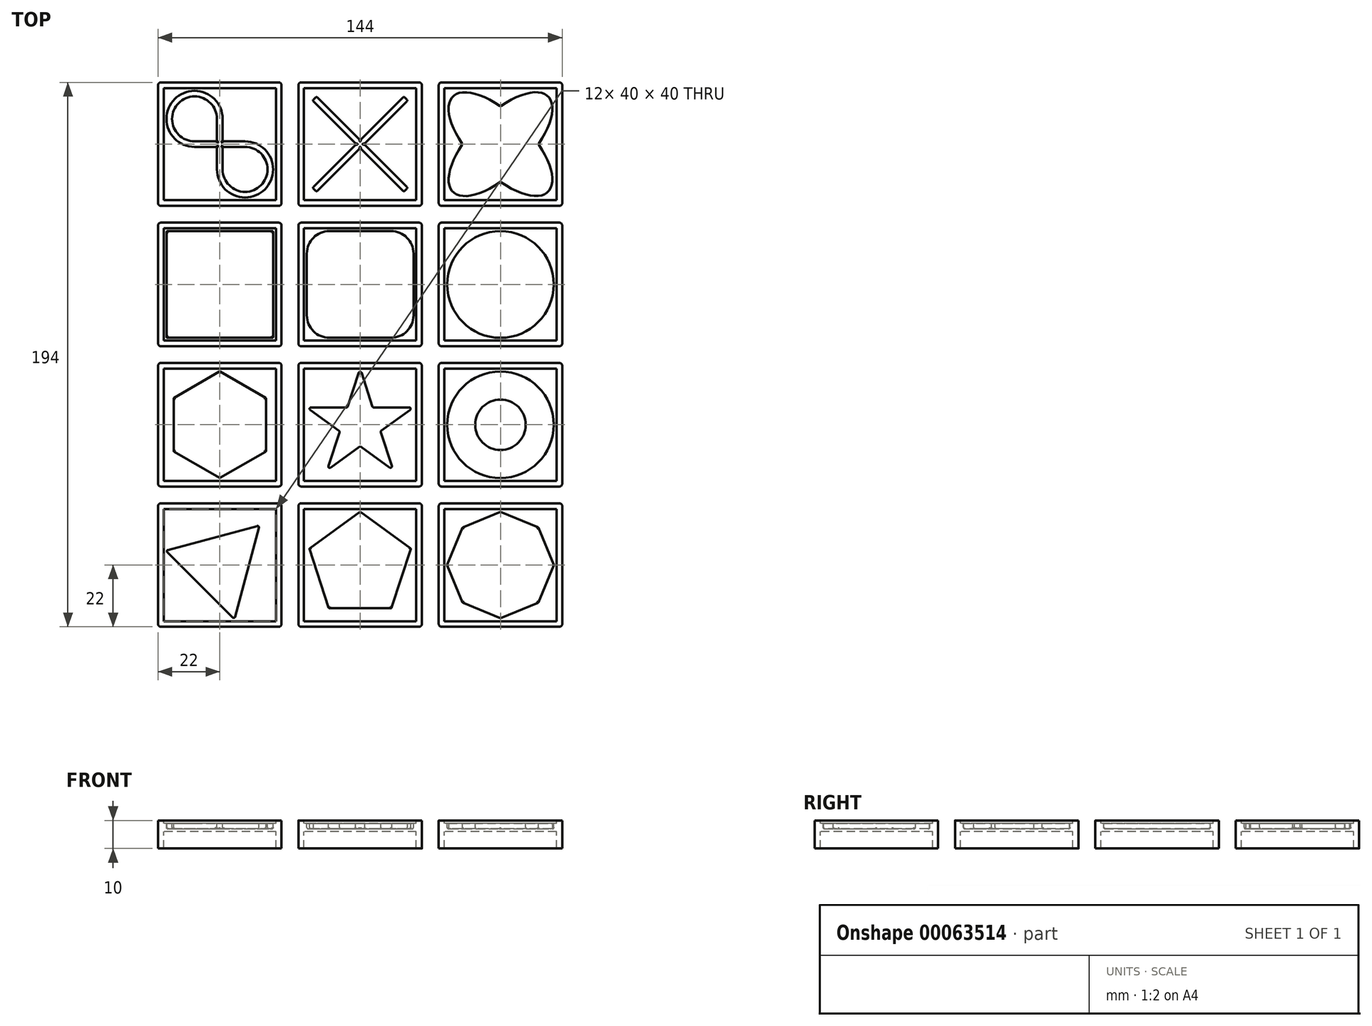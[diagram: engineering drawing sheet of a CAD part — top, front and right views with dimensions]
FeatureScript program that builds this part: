
annotation { "Feature Type Name" : "Feature", "Feature Type Description" : "" }
export const myFeature = defineFeature(function(context is Context, id is Id, definition is map)
    precondition{}
    {
        {
            var Q0;
            Q0=qCreatedBy(makeId("Top.planeOp"),FACE);
            var sketch = newSketch(context, id + "F0", { "sketchPlane" : qUnion([Q0])});
            skLineSegment(sketch, "E0.rect.bottom", {"start": v(20, 20) * mm, "end": v(-20, 20) * mm});
            skLineSegment(sketch, "E0.rect.top", {"start": v(20, -20) * mm, "end": v(-20, -20) * mm});
            skLineSegment(sketch, "E0.rect.left", {"start": v(20, 20) * mm, "end": v(20, -20) * mm});
            skLineSegment(sketch, "E0.rect.right", {"start": v(-20, 20) * mm, "end": v(-20, -20) * mm});
            skPoint(sketch, "E0.rect.middle", {"position": v(0, 0) * mm});
            skLineSegment(sketch, "E1.0.1.0", {"start": v(20, 30) * mm, "end": v(-20, 30) * mm});
            skLineSegment(sketch, "E1.0.1.1", {"start": v(-20, 70) * mm, "end": v(-20, 30) * mm});
            skLineSegment(sketch, "E1.0.1.2", {"start": v(20, 70) * mm, "end": v(-20, 70) * mm});
            skLineSegment(sketch, "E1.0.1.3", {"start": v(20, 70) * mm, "end": v(20, 30) * mm});
            skLineSegment(sketch, "E1.0.2.0", {"start": v(20, 80) * mm, "end": v(-20, 80) * mm});
            skLineSegment(sketch, "E1.0.2.1", {"start": v(-20, 120) * mm, "end": v(-20, 80) * mm});
            skLineSegment(sketch, "E1.0.2.2", {"start": v(20, 120) * mm, "end": v(-20, 120) * mm});
            skLineSegment(sketch, "E1.0.2.3", {"start": v(20, 120) * mm, "end": v(20, 80) * mm});
            skLineSegment(sketch, "E1.1.0.0", {"start": v(70, -20) * mm, "end": v(30, -20) * mm});
            skLineSegment(sketch, "E1.1.0.1", {"start": v(30, 20) * mm, "end": v(30, -20) * mm});
            skLineSegment(sketch, "E1.1.0.2", {"start": v(70, 20) * mm, "end": v(30, 20) * mm});
            skLineSegment(sketch, "E1.1.0.3", {"start": v(70, 20) * mm, "end": v(70, -20) * mm});
            skLineSegment(sketch, "E1.1.1.0", {"start": v(70, 30) * mm, "end": v(30, 30) * mm});
            skLineSegment(sketch, "E1.1.1.1", {"start": v(30, 70) * mm, "end": v(30, 30) * mm});
            skLineSegment(sketch, "E1.1.1.2", {"start": v(70, 70) * mm, "end": v(30, 70) * mm});
            skLineSegment(sketch, "E1.1.1.3", {"start": v(70, 70) * mm, "end": v(70, 30) * mm});
            skLineSegment(sketch, "E1.1.2.0", {"start": v(70, 80) * mm, "end": v(30, 80) * mm});
            skLineSegment(sketch, "E1.1.2.1", {"start": v(30, 120) * mm, "end": v(30, 80) * mm});
            skLineSegment(sketch, "E1.1.2.2", {"start": v(70, 120) * mm, "end": v(30, 120) * mm});
            skLineSegment(sketch, "E1.1.2.3", {"start": v(70, 120) * mm, "end": v(70, 80) * mm});
            skLineSegment(sketch, "E1.2.0.0", {"start": v(120, -20) * mm, "end": v(80, -20) * mm});
            skLineSegment(sketch, "E1.2.0.1", {"start": v(80, 20) * mm, "end": v(80, -20) * mm});
            skLineSegment(sketch, "E1.2.0.2", {"start": v(120, 20) * mm, "end": v(80, 20) * mm});
            skLineSegment(sketch, "E1.2.0.3", {"start": v(120, 20) * mm, "end": v(120, -20) * mm});
            skLineSegment(sketch, "E1.2.1.0", {"start": v(120, 30) * mm, "end": v(80, 30) * mm});
            skLineSegment(sketch, "E1.2.1.1", {"start": v(80, 70) * mm, "end": v(80, 30) * mm});
            skLineSegment(sketch, "E1.2.1.2", {"start": v(120, 70) * mm, "end": v(80, 70) * mm});
            skLineSegment(sketch, "E1.2.1.3", {"start": v(120, 70) * mm, "end": v(120, 30) * mm});
            skLineSegment(sketch, "E1.2.2.0", {"start": v(120, 80) * mm, "end": v(80, 80) * mm});
            skLineSegment(sketch, "E1.2.2.1", {"start": v(80, 120) * mm, "end": v(80, 80) * mm});
            skLineSegment(sketch, "E1.2.2.2", {"start": v(120, 120) * mm, "end": v(80, 120) * mm});
            skLineSegment(sketch, "E1.2.2.3", {"start": v(120, 120) * mm, "end": v(120, 80) * mm});
            skLineSegment(sketch, "E1.direction1", {"start": v(-20, -20) * mm, "end": v(30, -20) * mm, "construction": true});
            skLineSegment(sketch, "E1.direction2", {"start": v(-20, -20) * mm, "end": v(-20, 30) * mm, "construction": true});
            skLineSegment(sketch, "E2", {"start": v(-22, 122) * mm, "end": v(-20, 120) * mm, "construction": true});
            skLineSegment(sketch, "E3", {"start": v(120, -20) * mm, "end": v(122, -22) * mm, "construction": true});
            skLineSegment(sketch, "E4", {"start": v(122, 122) * mm, "end": v(120, 120) * mm, "construction": true});
            skLineSegment(sketch, "E5.0", {"start": v(-22, 22) * mm, "end": v(-22, -22) * mm});
            skLineSegment(sketch, "E5.1", {"start": v(22, 22) * mm, "end": v(-22, 22) * mm});
            skLineSegment(sketch, "E5.2", {"start": v(22, 22) * mm, "end": v(22, -22) * mm});
            skLineSegment(sketch, "E5.3", {"start": v(22, -22) * mm, "end": v(-22, -22) * mm});
            skLineSegment(sketch, "E6.0.1.0", {"start": v(-22, 72) * mm, "end": v(-22, 28) * mm});
            skLineSegment(sketch, "E6.0.1.1", {"start": v(22, 28) * mm, "end": v(-22, 28) * mm});
            skLineSegment(sketch, "E6.0.1.2", {"start": v(22, 72) * mm, "end": v(22, 28) * mm});
            skLineSegment(sketch, "E6.0.1.3", {"start": v(22, 72) * mm, "end": v(-22, 72) * mm});
            skLineSegment(sketch, "E6.0.2.0", {"start": v(-22, 122) * mm, "end": v(-22, 78) * mm});
            skLineSegment(sketch, "E6.0.2.1", {"start": v(22, 78) * mm, "end": v(-22, 78) * mm});
            skLineSegment(sketch, "E6.0.2.2", {"start": v(22, 122) * mm, "end": v(22, 78) * mm});
            skLineSegment(sketch, "E6.0.2.3", {"start": v(22, 122) * mm, "end": v(-22, 122) * mm});
            skLineSegment(sketch, "E6.1.0.0", {"start": v(28, 22) * mm, "end": v(28, -22) * mm});
            skLineSegment(sketch, "E6.1.0.1", {"start": v(72, -22) * mm, "end": v(28, -22) * mm});
            skLineSegment(sketch, "E6.1.0.2", {"start": v(72, 22) * mm, "end": v(72, -22) * mm});
            skLineSegment(sketch, "E6.1.0.3", {"start": v(72, 22) * mm, "end": v(28, 22) * mm});
            skLineSegment(sketch, "E6.1.1.0", {"start": v(28, 72) * mm, "end": v(28, 28) * mm});
            skLineSegment(sketch, "E6.1.1.1", {"start": v(72, 28) * mm, "end": v(28, 28) * mm});
            skLineSegment(sketch, "E6.1.1.2", {"start": v(72, 72) * mm, "end": v(72, 28) * mm});
            skLineSegment(sketch, "E6.1.1.3", {"start": v(72, 72) * mm, "end": v(28, 72) * mm});
            skLineSegment(sketch, "E6.1.2.0", {"start": v(28, 122) * mm, "end": v(28, 78) * mm});
            skLineSegment(sketch, "E6.1.2.1", {"start": v(72, 78) * mm, "end": v(28, 78) * mm});
            skLineSegment(sketch, "E6.1.2.2", {"start": v(72, 122) * mm, "end": v(72, 78) * mm});
            skLineSegment(sketch, "E6.1.2.3", {"start": v(72, 122) * mm, "end": v(28, 122) * mm});
            skLineSegment(sketch, "E6.2.0.0", {"start": v(78, 22) * mm, "end": v(78, -22) * mm});
            skLineSegment(sketch, "E6.2.0.1", {"start": v(122, -22) * mm, "end": v(78, -22) * mm});
            skLineSegment(sketch, "E6.2.0.2", {"start": v(122, 22) * mm, "end": v(122, -22) * mm});
            skLineSegment(sketch, "E6.2.0.3", {"start": v(122, 22) * mm, "end": v(78, 22) * mm});
            skLineSegment(sketch, "E6.2.1.0", {"start": v(78, 72) * mm, "end": v(78, 28) * mm});
            skLineSegment(sketch, "E6.2.1.1", {"start": v(122, 28) * mm, "end": v(78, 28) * mm});
            skLineSegment(sketch, "E6.2.1.2", {"start": v(122, 72) * mm, "end": v(122, 28) * mm});
            skLineSegment(sketch, "E6.2.1.3", {"start": v(122, 72) * mm, "end": v(78, 72) * mm});
            skLineSegment(sketch, "E6.2.2.0", {"start": v(78, 122) * mm, "end": v(78, 78) * mm});
            skLineSegment(sketch, "E6.2.2.1", {"start": v(122, 78) * mm, "end": v(78, 78) * mm});
            skLineSegment(sketch, "E6.2.2.2", {"start": v(122, 122) * mm, "end": v(122, 78) * mm});
            skLineSegment(sketch, "E6.2.2.3", {"start": v(122, 122) * mm, "end": v(78, 122) * mm});
            skLineSegment(sketch, "E6.direction1", {"start": v(-22, -22) * mm, "end": v(28, -22) * mm, "construction": true});
            skLineSegment(sketch, "E6.direction2", {"start": v(-22, -22) * mm, "end": v(-22, 28) * mm, "construction": true});
            skLineSegment(sketch, "E7.0.0.3", {"start": v(20, 130) * mm, "end": v(-20, 130) * mm});
            skLineSegment(sketch, "E7.3.0.3", {"start": v(-20, 170) * mm, "end": v(-20, 130) * mm});
            skLineSegment(sketch, "E7.6.0.3", {"start": v(20, 170) * mm, "end": v(-20, 170) * mm});
            skLineSegment(sketch, "E7.9.0.3", {"start": v(20, 170) * mm, "end": v(20, 130) * mm});
            skLineSegment(sketch, "E7.0.1.3", {"start": v(70, 130) * mm, "end": v(30, 130) * mm});
            skLineSegment(sketch, "E7.3.1.3", {"start": v(30, 170) * mm, "end": v(30, 130) * mm});
            skLineSegment(sketch, "E7.6.1.3", {"start": v(70, 170) * mm, "end": v(30, 170) * mm});
            skLineSegment(sketch, "E7.9.1.3", {"start": v(70, 170) * mm, "end": v(70, 130) * mm});
            skLineSegment(sketch, "E7.0.2.3", {"start": v(120, 130) * mm, "end": v(80, 130) * mm});
            skLineSegment(sketch, "E7.3.2.3", {"start": v(80, 170) * mm, "end": v(80, 130) * mm});
            skLineSegment(sketch, "E7.6.2.3", {"start": v(120, 170) * mm, "end": v(80, 170) * mm});
            skLineSegment(sketch, "E7.9.2.3", {"start": v(120, 170) * mm, "end": v(120, 130) * mm});
            skLineSegment(sketch, "E8.0.0.3", {"start": v(-22, 172) * mm, "end": v(-22, 128) * mm});
            skLineSegment(sketch, "E8.3.0.3", {"start": v(22, 128) * mm, "end": v(-22, 128) * mm});
            skLineSegment(sketch, "E8.6.0.3", {"start": v(22, 172) * mm, "end": v(22, 128) * mm});
            skLineSegment(sketch, "E8.9.0.3", {"start": v(22, 172) * mm, "end": v(-22, 172) * mm});
            skLineSegment(sketch, "E8.0.1.3", {"start": v(28, 172) * mm, "end": v(28, 128) * mm});
            skLineSegment(sketch, "E8.3.1.3", {"start": v(72, 128) * mm, "end": v(28, 128) * mm});
            skLineSegment(sketch, "E8.6.1.3", {"start": v(72, 172) * mm, "end": v(72, 128) * mm});
            skLineSegment(sketch, "E8.9.1.3", {"start": v(72, 172) * mm, "end": v(28, 172) * mm});
            skLineSegment(sketch, "E8.0.2.3", {"start": v(78, 172) * mm, "end": v(78, 128) * mm});
            skLineSegment(sketch, "E8.3.2.3", {"start": v(122, 128) * mm, "end": v(78, 128) * mm});
            skLineSegment(sketch, "E8.6.2.3", {"start": v(122, 172) * mm, "end": v(122, 128) * mm});
            skLineSegment(sketch, "E8.9.2.3", {"start": v(122, 172) * mm, "end": v(78, 172) * mm});
            skSolve(sketch);
        }
        {
            var Q0;
            Q0=qCreatedBy(makeId("Top.planeOp"),FACE);
            var sketch = newSketch(context, id + "F1", { "sketchPlane" : qUnion([Q0])});
            skLineSegment(sketch, "E9.0.0", {"start": v(-20, 80) * mm, "end": v(20, 80) * mm, "construction": true});
            skLineSegment(sketch, "E9.0.1", {"start": v(20, 80) * mm, "end": v(20, 120) * mm, "construction": true});
            skLineSegment(sketch, "E9.0.2", {"start": v(20, 120) * mm, "end": v(-20, 120) * mm, "construction": true});
            skLineSegment(sketch, "E9.0.3", {"start": v(-20, 120) * mm, "end": v(-20, 80) * mm, "construction": true});
            skLineSegment(sketch, "E9.1.0", {"start": v(30, 80) * mm, "end": v(70, 80) * mm, "construction": true});
            skLineSegment(sketch, "E9.1.1", {"start": v(70, 80) * mm, "end": v(70, 120) * mm, "construction": true});
            skLineSegment(sketch, "E9.1.2", {"start": v(70, 120) * mm, "end": v(30, 120) * mm, "construction": true});
            skLineSegment(sketch, "E9.1.3", {"start": v(30, 120) * mm, "end": v(30, 80) * mm, "construction": true});
            skLineSegment(sketch, "E9.2.0", {"start": v(80, 80) * mm, "end": v(120, 80) * mm, "construction": true});
            skLineSegment(sketch, "E9.2.1", {"start": v(120, 80) * mm, "end": v(120, 120) * mm, "construction": true});
            skLineSegment(sketch, "E9.2.2", {"start": v(120, 120) * mm, "end": v(80, 120) * mm, "construction": true});
            skLineSegment(sketch, "E9.2.3", {"start": v(80, 120) * mm, "end": v(80, 80) * mm, "construction": true});
            skLineSegment(sketch, "E9.3.0", {"start": v(80, 30) * mm, "end": v(120, 30) * mm, "construction": true});
            skLineSegment(sketch, "E9.3.1", {"start": v(120, 30) * mm, "end": v(120, 70) * mm, "construction": true});
            skLineSegment(sketch, "E9.3.2", {"start": v(120, 70) * mm, "end": v(80, 70) * mm, "construction": true});
            skLineSegment(sketch, "E9.3.3", {"start": v(80, 70) * mm, "end": v(80, 30) * mm, "construction": true});
            skLineSegment(sketch, "E9.4.0", {"start": v(30, 30) * mm, "end": v(70, 30) * mm, "construction": true});
            skLineSegment(sketch, "E9.4.1", {"start": v(70, 30) * mm, "end": v(70, 70) * mm, "construction": true});
            skLineSegment(sketch, "E9.4.2", {"start": v(70, 70) * mm, "end": v(30, 70) * mm, "construction": true});
            skLineSegment(sketch, "E9.4.3", {"start": v(30, 70) * mm, "end": v(30, 30) * mm, "construction": true});
            skLineSegment(sketch, "E9.5.0", {"start": v(-20, 30) * mm, "end": v(20, 30) * mm, "construction": true});
            skLineSegment(sketch, "E9.5.1", {"start": v(20, 30) * mm, "end": v(20, 70) * mm, "construction": true});
            skLineSegment(sketch, "E9.5.2", {"start": v(20, 70) * mm, "end": v(-20, 70) * mm, "construction": true});
            skLineSegment(sketch, "E9.5.3", {"start": v(-20, 70) * mm, "end": v(-20, 30) * mm, "construction": true});
            skPoint(sketch, "E9.6", {"position": v(0, 0) * mm});
            skLineSegment(sketch, "E9.7.0", {"start": v(30, -20) * mm, "end": v(70, -20) * mm, "construction": true});
            skLineSegment(sketch, "E9.7.1", {"start": v(70, -20) * mm, "end": v(70, 20) * mm, "construction": true});
            skLineSegment(sketch, "E9.7.2", {"start": v(70, 20) * mm, "end": v(30, 20) * mm, "construction": true});
            skLineSegment(sketch, "E9.7.3", {"start": v(30, 20) * mm, "end": v(30, -20) * mm, "construction": true});
            skLineSegment(sketch, "E9.8.0", {"start": v(80, -20) * mm, "end": v(120, -20) * mm, "construction": true});
            skLineSegment(sketch, "E9.8.1", {"start": v(120, -20) * mm, "end": v(120, 20) * mm, "construction": true});
            skLineSegment(sketch, "E9.8.2", {"start": v(120, 20) * mm, "end": v(80, 20) * mm, "construction": true});
            skLineSegment(sketch, "E9.8.3", {"start": v(80, 20) * mm, "end": v(80, -20) * mm, "construction": true});
            skLineSegment(sketch, "E9.9.0", {"start": v(20, -20) * mm, "end": v(20, 20) * mm, "construction": true});
            skLineSegment(sketch, "E9.9.1", {"start": v(20, 20) * mm, "end": v(-20, 20) * mm, "construction": true});
            skLineSegment(sketch, "E9.9.2", {"start": v(-20, 20) * mm, "end": v(-20, -20) * mm, "construction": true});
            skLineSegment(sketch, "E9.9.3", {"start": v(-20, -20) * mm, "end": v(20, -20) * mm, "construction": true});
            skLineSegment(sketch, "E10.0", {"start": v(19, 81.3) * mm, "end": v(19, 118.7) * mm});
            skLineSegment(sketch, "E10.1", {"start": v(-18.7, 81) * mm, "end": v(18.7, 81) * mm});
            skLineSegment(sketch, "E10.2", {"start": v(-19, 118.7) * mm, "end": v(-19, 81.3) * mm});
            skLineSegment(sketch, "E10.3", {"start": v(18.7, 119) * mm, "end": v(-18.7, 119) * mm});
            skLineSegment(sketch, "E11.0", {"start": v(61, 119) * mm, "end": v(39, 119) * mm});
            skLineSegment(sketch, "E11.1", {"start": v(69, 89) * mm, "end": v(69, 111) * mm});
            skLineSegment(sketch, "E11.2", {"start": v(39, 81) * mm, "end": v(61, 81) * mm});
            skLineSegment(sketch, "E11.3", {"start": v(31, 111) * mm, "end": v(31, 89) * mm});
            skPoint(sketch, "E12.visualSharp", {"position": v(31, 119) * mm});
            skArc(sketch, "E12.filletArc", {"start": v(39, 119) * mm, "mid": v(33.34, 116.66) * mm, "end": v(31, 111) * mm});
            skPoint(sketch, "E13.visualSharp", {"position": v(69, 119) * mm});
            skArc(sketch, "E13.filletArc", {"start": v(69, 111) * mm, "mid": v(66.66, 116.66) * mm, "end": v(61, 119) * mm});
            skPoint(sketch, "E14.visualSharp", {"position": v(69, 81) * mm});
            skArc(sketch, "E14.filletArc", {"start": v(61, 81) * mm, "mid": v(66.66, 83.34) * mm, "end": v(69, 89) * mm});
            skPoint(sketch, "E15.visualSharp", {"position": v(31, 81) * mm});
            skArc(sketch, "E15.filletArc", {"start": v(31, 89) * mm, "mid": v(33.34, 83.34) * mm, "end": v(39, 81) * mm});
            skCircle(sketch, "E16", {"center": v(100, 100) * mm, "radius": 19 * mm});
            skPoint(sketch, "E16.centerSnap0", {"position": v(100, 120) * mm});
            skPoint(sketch, "E16.centerSnap1", {"position": v(80, 100) * mm});
            skCircle(sketch, "E17", {"center": v(100, 50) * mm, "radius": 19 * mm});
            skPoint(sketch, "E17.centerSnap0", {"position": v(80, 50) * mm});
            skPoint(sketch, "E17.centerSnap1", {"position": v(100, 70) * mm});
            skCircle(sketch, "E18", {"center": v(100, 50) * mm, "radius": 9 * mm});
            skCircle(sketch, "E19.cCircle", {"center": v(50, 50) * mm, "radius": 20 * mm, "construction": true});
            skPoint(sketch, "E19.cCircle.centerSnap0", {"position": v(50, 70) * mm});
            skPoint(sketch, "E19.cCircle.centerSnap1", {"position": v(30, 50) * mm});
            skLineSegment(sketch, "E19.0", {"start": v(61.76, 33.82) * mm, "end": v(38.24, 33.82) * mm, "construction": true});
            skLineSegment(sketch, "E19.1", {"start": v(38.24, 33.82) * mm, "end": v(30.98, 56.18) * mm, "construction": true});
            skLineSegment(sketch, "E19.2", {"start": v(30.98, 56.18) * mm, "end": v(50, 70) * mm, "construction": true});
            skLineSegment(sketch, "E19.3", {"start": v(50, 70) * mm, "end": v(69.02, 56.18) * mm, "construction": true});
            skLineSegment(sketch, "E19.4", {"start": v(69.02, 56.18) * mm, "end": v(61.76, 33.82) * mm, "construction": true});
            skLineSegment(sketch, "E20", {"start": v(49.52, 68.54) * mm, "end": v(45.62, 56.53) * mm});
            skLineSegment(sketch, "E21", {"start": v(39.49, 34.72) * mm, "end": v(49.7, 42.15) * mm});
            skLineSegment(sketch, "E22", {"start": v(50.48, 68.54) * mm, "end": v(54.38, 56.53) * mm});
            skLineSegment(sketch, "E23", {"start": v(32.22, 55.28) * mm, "end": v(42.44, 47.85) * mm});
            skLineSegment(sketch, "E24", {"start": v(32.52, 56.18) * mm, "end": v(45.15, 56.18) * mm});
            skLineSegment(sketch, "E25.trimOffspring", {"start": v(54.85, 56.18) * mm, "end": v(67.48, 56.18) * mm});
            skLineSegment(sketch, "E26.trimOffspring", {"start": v(42.62, 47.3) * mm, "end": v(38.72, 35.28) * mm});
            skLineSegment(sketch, "E27.trimOffspring", {"start": v(50.3, 42.15) * mm, "end": v(60.51, 34.72) * mm});
            skLineSegment(sketch, "E28.trimOffspring", {"start": v(57.38, 47.3) * mm, "end": v(61.28, 35.28) * mm});
            skLineSegment(sketch, "E29.trimOffspring", {"start": v(57.56, 47.85) * mm, "end": v(67.78, 55.28) * mm});
            skArc(sketch, "E30.filletArc", {"start": v(50.48, 68.54) * mm, "mid": v(50, 68.88) * mm, "end": v(49.52, 68.54) * mm});
            skPoint(sketch, "E31.visualSharp", {"position": v(54.5, 56.18) * mm});
            skArc(sketch, "E31.filletArc", {"start": v(54.38, 56.53) * mm, "mid": v(54.56, 56.28) * mm, "end": v(54.85, 56.18) * mm});
            skPoint(sketch, "E32.visualSharp", {"position": v(69.02, 56.18) * mm});
            skArc(sketch, "E32.filletArc", {"start": v(67.78, 55.28) * mm, "mid": v(67.96, 55.83) * mm, "end": v(67.48, 56.18) * mm});
            skPoint(sketch, "E33.visualSharp", {"position": v(57.27, 47.64) * mm});
            skArc(sketch, "E33.filletArc", {"start": v(57.56, 47.85) * mm, "mid": v(57.38, 47.6) * mm, "end": v(57.38, 47.3) * mm});
            skPoint(sketch, "E34.visualSharp", {"position": v(61.76, 33.82) * mm});
            skArc(sketch, "E34.filletArc", {"start": v(60.51, 34.72) * mm, "mid": v(61.1, 34.72) * mm, "end": v(61.28, 35.28) * mm});
            skPoint(sketch, "E35.visualSharp", {"position": v(50, 42.36) * mm});
            skArc(sketch, "E35.filletArc", {"start": v(50.3, 42.15) * mm, "mid": v(50, 42.24) * mm, "end": v(49.7, 42.15) * mm});
            skPoint(sketch, "E36.visualSharp", {"position": v(38.24, 33.82) * mm});
            skArc(sketch, "E36.filletArc", {"start": v(38.72, 35.28) * mm, "mid": v(38.9, 34.72) * mm, "end": v(39.49, 34.72) * mm});
            skPoint(sketch, "E37.visualSharp", {"position": v(42.73, 47.64) * mm});
            skArc(sketch, "E37.filletArc", {"start": v(42.62, 47.3) * mm, "mid": v(42.62, 47.6) * mm, "end": v(42.44, 47.85) * mm});
            skPoint(sketch, "E38.visualSharp", {"position": v(30.98, 56.18) * mm});
            skArc(sketch, "E38.filletArc", {"start": v(32.52, 56.18) * mm, "mid": v(32.04, 55.83) * mm, "end": v(32.22, 55.28) * mm});
            skPoint(sketch, "E39.visualSharp", {"position": v(45.5, 56.18) * mm});
            skArc(sketch, "E39.filletArc", {"start": v(45.15, 56.18) * mm, "mid": v(45.44, 56.28) * mm, "end": v(45.62, 56.53) * mm});
            skPoint(sketch, "E40.visualSharp", {"position": v(19, 119) * mm});
            skArc(sketch, "E40.filletArc", {"start": v(19, 118.7) * mm, "mid": v(18.91, 118.91) * mm, "end": v(18.7, 119) * mm});
            skPoint(sketch, "E41.visualSharp", {"position": v(19, 81) * mm});
            skArc(sketch, "E41.filletArc", {"start": v(18.7, 81) * mm, "mid": v(18.91, 81.09) * mm, "end": v(19, 81.3) * mm});
            skPoint(sketch, "E42.visualSharp", {"position": v(-19, 81) * mm});
            skArc(sketch, "E42.filletArc", {"start": v(-19, 81.3) * mm, "mid": v(-18.91, 81.09) * mm, "end": v(-18.7, 81) * mm});
            skPoint(sketch, "E43.visualSharp", {"position": v(-19, 119) * mm});
            skArc(sketch, "E43.filletArc", {"start": v(-18.7, 119) * mm, "mid": v(-18.91, 118.91) * mm, "end": v(-19, 118.7) * mm});
            skCircle(sketch, "E44.cCircle", {"center": v(0, 0) * mm, "radius": 20 * mm, "construction": true});
            skLineSegment(sketch, "E44.0", {"start": v(4.56, -18.7) * mm, "end": v(-18.7, 4.56) * mm});
            skLineSegment(sketch, "E44.1", {"start": v(-18.48, 5.4) * mm, "end": v(13.3, 13.92) * mm});
            skLineSegment(sketch, "E44.2", {"start": v(13.92, 13.3) * mm, "end": v(5.4, -18.48) * mm});
            skLineSegment(sketch, "E45", {"start": v(-20, -20) * mm, "end": v(20, 20) * mm, "construction": true});
            skPoint(sketch, "E46.visualSharp", {"position": v(-19.32, 5.18) * mm});
            skArc(sketch, "E46.filletArc", {"start": v(-18.48, 5.4) * mm, "mid": v(-18.84, 5.05) * mm, "end": v(-18.7, 4.56) * mm});
            skPoint(sketch, "E47.visualSharp", {"position": v(14.14, 14.14) * mm});
            skArc(sketch, "E47.filletArc", {"start": v(13.92, 13.3) * mm, "mid": v(13.79, 13.79) * mm, "end": v(13.3, 13.92) * mm});
            skPoint(sketch, "E48.visualSharp", {"position": v(5.18, -19.32) * mm});
            skArc(sketch, "E48.filletArc", {"start": v(4.56, -18.7) * mm, "mid": v(5.05, -18.84) * mm, "end": v(5.4, -18.48) * mm});
            skCircle(sketch, "E49.cCircle", {"center": v(0, 50) * mm, "radius": 19 * mm, "construction": true});
            skPoint(sketch, "E49.cCircle.centerSnap0", {"position": v(0, 70) * mm});
            skPoint(sketch, "E49.cCircle.centerSnap1", {"position": v(-20, 50) * mm});
            skLineSegment(sketch, "E49.0", {"start": v(-0.15, 31.09) * mm, "end": v(-16.3, 40.41) * mm});
            skLineSegment(sketch, "E49.1", {"start": v(-16.45, 40.67) * mm, "end": v(-16.45, 59.33) * mm});
            skLineSegment(sketch, "E49.2", {"start": v(-16.3, 59.59) * mm, "end": v(-0.15, 68.91) * mm});
            skLineSegment(sketch, "E49.3", {"start": v(0.15, 68.91) * mm, "end": v(16.3, 59.59) * mm});
            skLineSegment(sketch, "E49.4", {"start": v(16.45, 59.33) * mm, "end": v(16.45, 40.67) * mm});
            skLineSegment(sketch, "E49.5", {"start": v(16.3, 40.41) * mm, "end": v(0.15, 31.09) * mm});
            skPoint(sketch, "E50.visualSharp", {"position": v(-16.45, 59.5) * mm});
            skArc(sketch, "E50.filletArc", {"start": v(-16.3, 59.59) * mm, "mid": v(-16.41, 59.48) * mm, "end": v(-16.45, 59.33) * mm});
            skPoint(sketch, "E51.visualSharp", {"position": v(-16.45, 40.5) * mm});
            skArc(sketch, "E51.filletArc", {"start": v(-16.45, 40.67) * mm, "mid": v(-16.41, 40.52) * mm, "end": v(-16.3, 40.41) * mm});
            skPoint(sketch, "E52.visualSharp", {"position": v(0, 31) * mm});
            skArc(sketch, "E52.filletArc", {"start": v(-0.15, 31.09) * mm, "mid": v(0, 31.05) * mm, "end": v(0.15, 31.09) * mm});
            skPoint(sketch, "E53.visualSharp", {"position": v(16.45, 40.5) * mm});
            skArc(sketch, "E53.filletArc", {"start": v(16.3, 40.41) * mm, "mid": v(16.41, 40.52) * mm, "end": v(16.45, 40.67) * mm});
            skPoint(sketch, "E54.visualSharp", {"position": v(16.45, 59.5) * mm});
            skArc(sketch, "E54.filletArc", {"start": v(16.45, 59.33) * mm, "mid": v(16.41, 59.48) * mm, "end": v(16.3, 59.59) * mm});
            skPoint(sketch, "E55.visualSharp", {"position": v(0, 69) * mm});
            skArc(sketch, "E55.filletArc", {"start": v(0.15, 68.91) * mm, "mid": v(0, 68.95) * mm, "end": v(-0.15, 68.91) * mm});
            skCircle(sketch, "E56.cCircle", {"center": v(50, 0) * mm, "radius": 19 * mm, "construction": true});
            skPoint(sketch, "E56.cCircle.centerSnap0", {"position": v(50, 20) * mm});
            skLineSegment(sketch, "E56.0", {"start": v(60.95, -15.37) * mm, "end": v(39.05, -15.37) * mm});
            skLineSegment(sketch, "E56.1", {"start": v(38.76, -15.16) * mm, "end": v(32, 5.66) * mm});
            skLineSegment(sketch, "E56.2", {"start": v(32.1, 6) * mm, "end": v(49.82, 18.87) * mm});
            skLineSegment(sketch, "E56.3", {"start": v(50.18, 18.87) * mm, "end": v(67.9, 6) * mm});
            skLineSegment(sketch, "E56.4", {"start": v(68, 5.66) * mm, "end": v(61.24, -15.16) * mm});
            skPoint(sketch, "E57.visualSharp", {"position": v(50, 19) * mm});
            skArc(sketch, "E57.filletArc", {"start": v(50.18, 18.87) * mm, "mid": v(50, 18.93) * mm, "end": v(49.82, 18.87) * mm});
            skPoint(sketch, "E58.visualSharp", {"position": v(68.07, 5.87) * mm});
            skArc(sketch, "E58.filletArc", {"start": v(68, 5.66) * mm, "mid": v(68, 5.85) * mm, "end": v(67.9, 6) * mm});
            skPoint(sketch, "E59.visualSharp", {"position": v(61.17, -15.37) * mm});
            skArc(sketch, "E59.filletArc", {"start": v(60.95, -15.37) * mm, "mid": v(61.13, -15.31) * mm, "end": v(61.24, -15.16) * mm});
            skPoint(sketch, "E60.visualSharp", {"position": v(38.83, -15.37) * mm});
            skArc(sketch, "E60.filletArc", {"start": v(38.76, -15.16) * mm, "mid": v(38.87, -15.31) * mm, "end": v(39.05, -15.37) * mm});
            skPoint(sketch, "E61.visualSharp", {"position": v(31.93, 5.87) * mm});
            skArc(sketch, "E61.filletArc", {"start": v(32.1, 6) * mm, "mid": v(32, 5.85) * mm, "end": v(32, 5.66) * mm});
            skCircle(sketch, "E62.cCircle", {"center": v(100, 0) * mm, "radius": 19 * mm, "construction": true});
            skPoint(sketch, "E62.cCircle.centerSnap0", {"position": v(100, 20) * mm});
            skPoint(sketch, "E62.cCircle.perimeterSnap0", {"position": v(100, 20) * mm});
            skLineSegment(sketch, "E62.0", {"start": v(99.89, -18.95) * mm, "end": v(86.68, -13.48) * mm});
            skPoint(sketch, "E62.0.startSnap0", {"position": v(100, 20) * mm});
            skLineSegment(sketch, "E62.1", {"start": v(86.52, -13.32) * mm, "end": v(81.05, -0.11) * mm});
            skLineSegment(sketch, "E62.2", {"start": v(81.05, 0.11) * mm, "end": v(86.52, 13.32) * mm});
            skLineSegment(sketch, "E62.3", {"start": v(86.68, 13.48) * mm, "end": v(99.89, 18.95) * mm});
            skLineSegment(sketch, "E62.4", {"start": v(100.11, 18.95) * mm, "end": v(113.32, 13.48) * mm});
            skLineSegment(sketch, "E62.5", {"start": v(113.48, 13.32) * mm, "end": v(118.95, 0.11) * mm});
            skLineSegment(sketch, "E62.6", {"start": v(118.95, -0.11) * mm, "end": v(113.48, -13.32) * mm});
            skLineSegment(sketch, "E62.7", {"start": v(113.32, -13.48) * mm, "end": v(100.11, -18.95) * mm});
            skPoint(sketch, "E63.visualSharp", {"position": v(86.56, 13.44) * mm});
            skArc(sketch, "E63.filletArc", {"start": v(86.68, 13.48) * mm, "mid": v(86.58, 13.42) * mm, "end": v(86.52, 13.32) * mm});
            skPoint(sketch, "E64.visualSharp", {"position": v(81, 0) * mm});
            skArc(sketch, "E64.filletArc", {"start": v(81.05, 0.11) * mm, "mid": v(81.02, 0) * mm, "end": v(81.05, -0.11) * mm});
            skPoint(sketch, "E65.visualSharp", {"position": v(86.56, -13.44) * mm});
            skArc(sketch, "E65.filletArc", {"start": v(86.52, -13.32) * mm, "mid": v(86.58, -13.42) * mm, "end": v(86.68, -13.48) * mm});
            skPoint(sketch, "E66.visualSharp", {"position": v(100, -19) * mm});
            skArc(sketch, "E66.filletArc", {"start": v(99.89, -18.95) * mm, "mid": v(100, -18.98) * mm, "end": v(100.11, -18.95) * mm});
            skPoint(sketch, "E67.visualSharp", {"position": v(113.44, -13.44) * mm});
            skArc(sketch, "E67.filletArc", {"start": v(113.32, -13.48) * mm, "mid": v(113.42, -13.42) * mm, "end": v(113.48, -13.32) * mm});
            skPoint(sketch, "E68.visualSharp", {"position": v(119, 0) * mm});
            skArc(sketch, "E68.filletArc", {"start": v(118.95, -0.11) * mm, "mid": v(118.98, 0) * mm, "end": v(118.95, 0.11) * mm});
            skPoint(sketch, "E69.visualSharp", {"position": v(113.44, 13.44) * mm});
            skArc(sketch, "E69.filletArc", {"start": v(113.48, 13.32) * mm, "mid": v(113.42, 13.42) * mm, "end": v(113.32, 13.48) * mm});
            skPoint(sketch, "E70.visualSharp", {"position": v(100, 19) * mm});
            skArc(sketch, "E70.filletArc", {"start": v(100.11, 18.95) * mm, "mid": v(100, 18.98) * mm, "end": v(99.89, 18.95) * mm});
            skLineSegment(sketch, "E71.0.0", {"start": v(80, 130) * mm, "end": v(120, 130) * mm});
            skLineSegment(sketch, "E71.0.1", {"start": v(120, 130) * mm, "end": v(120, 170) * mm});
            skLineSegment(sketch, "E71.0.2", {"start": v(120, 170) * mm, "end": v(80, 170) * mm});
            skLineSegment(sketch, "E71.0.3", {"start": v(80, 170) * mm, "end": v(80, 130) * mm});
            skLineSegment(sketch, "E72", {"start": v(120, 170) * mm, "end": v(80, 130) * mm, "construction": true});
            skLineSegment(sketch, "E73", {"start": v(120, 130) * mm, "end": v(80, 170) * mm, "construction": true});
            skPoint(sketch, "E74", {"position": v(100, 150) * mm});
            skEllipticalArc(sketch, "E75", {});
            skEllipticalArc(sketch, "E76.1.0", {});
            skEllipticalArc(sketch, "E77.trimOffspring", {});
            skEllipticalArc(sketch, "E78.trimOffspring", {});
            skPoint(sketch, "E79.visualSharp", {"position": v(100, 136.51) * mm});
            skArc(sketch, "E79.filletArc", {"start": v(100.18, 136.4) * mm, "mid": v(100, 136.45) * mm, "end": v(99.84, 136.4) * mm});
            skPoint(sketch, "E80.visualSharp", {"position": v(86.51, 150) * mm});
            skArc(sketch, "E80.filletArc", {"start": v(86.4, 149.82) * mm, "mid": v(86.45, 150) * mm, "end": v(86.4, 150.16) * mm});
            skPoint(sketch, "E81.visualSharp", {"position": v(100, 163.49) * mm});
            skArc(sketch, "E81.filletArc", {"start": v(99.82, 163.6) * mm, "mid": v(100, 163.55) * mm, "end": v(100.16, 163.6) * mm});
            skPoint(sketch, "E82.visualSharp", {"position": v(113.49, 150) * mm});
            skArc(sketch, "E82.filletArc", {"start": v(113.6, 150.18) * mm, "mid": v(113.55, 150) * mm, "end": v(113.6, 149.84) * mm});
            skLineSegment(sketch, "E83.0.0", {"start": v(30, 130) * mm, "end": v(70, 130) * mm});
            skLineSegment(sketch, "E83.0.2", {"start": v(70, 170) * mm, "end": v(30, 170) * mm});
            skLineSegment(sketch, "E83.0.3", {"start": v(30, 170) * mm, "end": v(30, 130) * mm});
            skLineSegment(sketch, "E84", {"start": v(30, 130) * mm, "end": v(70, 170) * mm, "construction": true});
            skLineSegment(sketch, "E85", {"start": v(70, 130) * mm, "end": v(30, 170) * mm, "construction": true});
            skLineSegment(sketch, "E86", {"start": v(33.03, 134.44) * mm, "end": v(34.44, 133.03) * mm});
            skLineSegment(sketch, "E87", {"start": v(34.44, 133.03) * mm, "end": v(50, 148.59) * mm});
            skLineSegment(sketch, "E88", {"start": v(50, 148.59) * mm, "end": v(65.56, 133.03) * mm});
            skLineSegment(sketch, "E89", {"start": v(65.56, 133.03) * mm, "end": v(66.97, 134.44) * mm});
            skLineSegment(sketch, "E90", {"start": v(66.97, 134.44) * mm, "end": v(51.41, 150) * mm});
            skLineSegment(sketch, "E91", {"start": v(51.41, 150) * mm, "end": v(66.97, 165.56) * mm});
            skLineSegment(sketch, "E92", {"start": v(66.97, 165.56) * mm, "end": v(65.56, 166.97) * mm});
            skLineSegment(sketch, "E93", {"start": v(65.56, 166.97) * mm, "end": v(50, 151.41) * mm});
            skLineSegment(sketch, "E94", {"start": v(50, 151.41) * mm, "end": v(34.44, 166.97) * mm});
            skLineSegment(sketch, "E95", {"start": v(34.44, 166.97) * mm, "end": v(33.03, 165.56) * mm});
            skLineSegment(sketch, "E96", {"start": v(33.03, 165.56) * mm, "end": v(48.59, 150) * mm});
            skLineSegment(sketch, "E97", {"start": v(48.59, 150) * mm, "end": v(33.03, 134.44) * mm});
            skLineSegment(sketch, "E98.0.0", {"start": v(-20, 130) * mm, "end": v(20, 130) * mm});
            skLineSegment(sketch, "E98.0.2", {"start": v(20, 170) * mm, "end": v(-20, 170) * mm});
            skLineSegment(sketch, "E98.0.3", {"start": v(-20, 170) * mm, "end": v(-20, 130) * mm});
            skLineSegment(sketch, "E99.0", {"start": v(19, 169) * mm, "end": v(-19, 169) * mm, "construction": true});
            skLineSegment(sketch, "E99.1", {"start": v(19, 131) * mm, "end": v(19, 169) * mm, "construction": true});
            skLineSegment(sketch, "E99.2", {"start": v(-19, 131) * mm, "end": v(19, 131) * mm, "construction": true});
            skLineSegment(sketch, "E99.3", {"start": v(-19, 169) * mm, "end": v(-19, 131) * mm, "construction": true});
            skLineSegment(sketch, "E100.rect.bottom", {"start": v(2, 159.5) * mm, "end": v(1.96, 159.5) * mm, "construction": true});
            skLineSegment(sketch, "E100.rect.right", {"start": v(-9.5, 148.04) * mm, "end": v(-9.5, 148) * mm, "construction": true});
            skLineSegment(sketch, "E101.trimOffspring", {"start": v(-0.9, 150.9) * mm, "end": v(-0.89, 150.89) * mm, "construction": true});
            skLineSegment(sketch, "E102.trimOffspring", {"start": v(-1.12, 148.88) * mm, "end": v(-1.1, 148.9) * mm, "construction": true});
            skLineSegment(sketch, "E103", {"start": v(-19, 150) * mm, "end": v(0, 150) * mm, "construction": true});
            skLineSegment(sketch, "E104", {"start": v(0, 131) * mm, "end": v(0, 150) * mm, "construction": true});
            skLineSegment(sketch, "E105", {"start": v(0, 150) * mm, "end": v(0, 169) * mm, "construction": true});
            skLineSegment(sketch, "E106", {"start": v(0, 150) * mm, "end": v(19, 150) * mm, "construction": true});
            skCircle(sketch, "E107", {"center": v(-9, 159) * mm, "radius": 9 * mm, "construction": true});
            skArc(sketch, "E108.0", {"start": v(-1, 159) * mm, "mid": v(-14.66, 164.66) * mm, "end": v(-9, 151) * mm});
            skLineSegment(sketch, "E109", {"start": v(-19, 131) * mm, "end": v(19, 169) * mm, "construction": true});
            skCircle(sketch, "E110.MirrorC", {"center": v(9, 141) * mm, "radius": 9 * mm, "construction": true});
            skArc(sketch, "E111.MirrorC", {"start": v(9, 149) * mm, "mid": v(14.66, 135.34) * mm, "end": v(1, 141) * mm});
            skArc(sketch, "E112.MirrorC", {"start": v(9, 151) * mm, "mid": v(16.07, 133.93) * mm, "end": v(-1, 141) * mm});
            skLineSegment(sketch, "E113.bottom", {"start": v(-9, 159) * mm, "end": v(9, 159) * mm, "construction": true});
            skLineSegment(sketch, "E113.top", {"start": v(-9, 141) * mm, "end": v(9, 141) * mm, "construction": true});
            skLineSegment(sketch, "E113.left", {"start": v(-9, 159) * mm, "end": v(-9, 141) * mm, "construction": true});
            skLineSegment(sketch, "E113.right", {"start": v(9, 159) * mm, "end": v(9, 141) * mm, "construction": true});
            skLineSegment(sketch, "E114", {"start": v(1, 159) * mm, "end": v(1, 151) * mm});
            skLineSegment(sketch, "E115", {"start": v(-1, 141) * mm, "end": v(-1, 149) * mm});
            skLineSegment(sketch, "E116", {"start": v(-9, 151) * mm, "end": v(-1, 151) * mm});
            skLineSegment(sketch, "E117", {"start": v(9, 149) * mm, "end": v(1, 149) * mm});
            skLineSegment(sketch, "E118.trimOffspring", {"start": v(1, 149) * mm, "end": v(1, 141) * mm});
            skLineSegment(sketch, "E119.trimOffspring", {"start": v(-1, 149) * mm, "end": v(-9, 149) * mm});
            skLineSegment(sketch, "E120.trimOffspring", {"start": v(-1, 151) * mm, "end": v(-1, 159) * mm});
            skLineSegment(sketch, "E121.trimOffspring", {"start": v(1, 151) * mm, "end": v(9, 151) * mm});
            skArc(sketch, "E122.trimOffspring", {"start": v(1, 159) * mm, "mid": v(-16.07, 166.07) * mm, "end": v(-9, 149) * mm});
            const initialGuessF1  = {"E75": [0.1, 0.15, -0.7075180190996215, 0.7066953039672386, 0.024, 0.01039352310790653, 5.1301685465043825, 1.1530167606752042], "E76.1.0": [0.1, 0.15, -0.7066953039672386, -0.7075180190996215, 0.024, 0.01039352310790653, 1.9885758929145876, 4.294609414265008], "E77.trimOffspring": [0.1, 0.15, -0.7066953039672386, -0.7075180190996215, 0.024, 0.01039352310790653, 5.130168546504371, 1.153016760675205], "E78.trimOffspring": [0.1, 0.15, -0.7075180190996215, 0.7066953039672386, 0.024, 0.01039352310790653, 1.9885758929145763, 4.2946094142650075]};
            skSetInitialGuess(sketch, initialGuessF1);
            skSolve(sketch);
        }
        {
            var Q0;
            Q0=makeQuery(id+"F0.imprint","IMPRINT",FACE,{"disambiguationData":[TD([[makeQuery(id+"F0.imprint","IMPRINT",EDGE,{"derivedFrom":sQuery(id+"F0.wireOp",EDGE,"E1.0.2.0")}),-1.0]])]});
            var Q1;
            Q1=makeQuery(id+"F0.imprint","IMPRINT",FACE,{"disambiguationData":[TD([[makeQuery(id+"F0.imprint","IMPRINT",EDGE,{"derivedFrom":sQuery(id+"F0.wireOp",EDGE,"E1.1.2.0")}),-1.0]])]});
            var Q2;
            Q2=makeQuery(id+"F0.imprint","IMPRINT",FACE,{"disambiguationData":[TD([[makeQuery(id+"F0.imprint","IMPRINT",EDGE,{"derivedFrom":sQuery(id+"F0.wireOp",EDGE,"E1.1.1.0")}),-1.0]])]});
            var Q3;
            Q3=makeQuery(id+"F0.imprint","IMPRINT",FACE,{"disambiguationData":[TD([[makeQuery(id+"F0.imprint","IMPRINT",EDGE,{"derivedFrom":sQuery(id+"F0.wireOp",EDGE,"E1.0.1.0")}),-1.0]])]});
            var Q4;
            Q4=makeQuery(id+"F0.imprint","IMPRINT",FACE,{"disambiguationData":[TD([[makeQuery(id+"F0.imprint","IMPRINT",EDGE,{"derivedFrom":sQuery(id+"F0.wireOp",EDGE,"E0.rect.bottom")}),1.0]])]});
            var Q5;
            Q5=makeQuery(id+"F0.imprint","IMPRINT",FACE,{"disambiguationData":[TD([[makeQuery(id+"F0.imprint","IMPRINT",EDGE,{"derivedFrom":sQuery(id+"F0.wireOp",EDGE,"E1.1.0.0")}),-1.0]])]});
            var Q6;
            Q6=makeQuery(id+"F0.imprint","IMPRINT",FACE,{"disambiguationData":[TD([[makeQuery(id+"F0.imprint","IMPRINT",EDGE,{"derivedFrom":sQuery(id+"F0.wireOp",EDGE,"E1.2.0.0")}),-1.0]])]});
            var Q7;
            Q7=makeQuery(id+"F0.imprint","IMPRINT",FACE,{"disambiguationData":[TD([[makeQuery(id+"F0.imprint","IMPRINT",EDGE,{"derivedFrom":sQuery(id+"F0.wireOp",EDGE,"E1.2.1.0")}),-1.0]])]});
            var Q8;
            Q8=makeQuery(id+"F0.imprint","IMPRINT",FACE,{"disambiguationData":[TD([[makeQuery(id+"F0.imprint","IMPRINT",EDGE,{"derivedFrom":sQuery(id+"F0.wireOp",EDGE,"E1.2.2.0")}),-1.0]])]});
            var Q9;
            Q9=makeQuery(id+"F0.imprint","IMPRINT",FACE,{"disambiguationData":[TD([[makeQuery(id+"F0.imprint","IMPRINT",EDGE,{"derivedFrom":sQuery(id+"F0.wireOp",EDGE,"E7.0.0.3")}),-1.0]])]});
            var Q10;
            Q10=makeQuery(id+"F0.imprint","IMPRINT",FACE,{"disambiguationData":[TD([[makeQuery(id+"F0.imprint","IMPRINT",EDGE,{"derivedFrom":sQuery(id+"F0.wireOp",EDGE,"E7.0.1.3")}),-1.0]])]});
            var Q11;
            Q11=makeQuery(id+"F0.imprint","IMPRINT",FACE,{"disambiguationData":[TD([[makeQuery(id+"F0.imprint","IMPRINT",EDGE,{"derivedFrom":sQuery(id+"F0.wireOp",EDGE,"E7.0.2.3")}),-1.0]])]});
            extrude(context, id + "F2", {"entities" : qUnion([Q0, Q1, Q2, Q3, Q4, Q5, Q6, Q7, Q8, Q9, Q10, Q11]), "oppositeDirection" : true, "depth" : 3 * mm});
        }
        {
            var Q0;
            Q0=makeQuery(id+"F1.imprint","IMPRINT",FACE,{"disambiguationData":[TD([[makeQuery(id+"F1.imprint","IMPRINT",EDGE,{"derivedFrom":sQuery(id+"F1.wireOp",EDGE,"E86")}),1.0]])]});
            extrude(context, id + "F3", {"entities" : qUnion([Q0]), "operationType" : NewBodyOperationType.REMOVE, "oppositeDirection" : true, "depth" : 2 * mm});
        }
        {
            var Q0;
            Q0=makeQuery(id+"F1.imprint","IMPRINT",FACE,{"disambiguationData":[TD([[makeQuery(id+"F1.imprint","IMPRINT",EDGE,{"derivedFrom":sQuery(id+"F1.wireOp",EDGE,"E10.0")}),1.0]])]});
            var Q1;
            Q1=makeQuery(id+"F1.imprint","IMPRINT",FACE,{"disambiguationData":[TD([[makeQuery(id+"F1.imprint","IMPRINT",EDGE,{"derivedFrom":sQuery(id+"F1.wireOp",EDGE,"E11.0")}),1.0]])]});
            var Q2;
            Q2=makeQuery(id+"F1.imprint","IMPRINT",FACE,{"disambiguationData":[TD([[makeQuery(id+"F1.imprint","IMPRINT",EDGE,{"derivedFrom":sQuery(id+"F1.wireOp",EDGE,"E16")}),1.0]])]});
            var Q3;
            Q3=makeQuery(id+"F1.imprint","IMPRINT",FACE,{"disambiguationData":[TD([[makeQuery(id+"F1.imprint","IMPRINT",EDGE,{"derivedFrom":sQuery(id+"F1.wireOp",EDGE,"E20")}),1.0]])]});
            var Q4;
            Q4=makeQuery(id+"F1.imprint","IMPRINT",FACE,{"disambiguationData":[TD([[makeQuery(id+"F1.imprint","IMPRINT",EDGE,{"derivedFrom":sQuery(id+"F1.wireOp",EDGE,"E44.0")}),-1.0]])]});
            var Q5;
            Q5=makeQuery(id+"F1.imprint","IMPRINT",FACE,{"disambiguationData":[TD([[makeQuery(id+"F1.imprint","IMPRINT",EDGE,{"derivedFrom":sQuery(id+"F1.wireOp",EDGE,"E49.0")}),-1.0]])]});
            var Q6;
            Q6=makeQuery(id+"F1.imprint","IMPRINT",FACE,{"disambiguationData":[TD([[makeQuery(id+"F1.imprint","IMPRINT",EDGE,{"derivedFrom":sQuery(id+"F1.wireOp",EDGE,"E56.0")}),-1.0]])]});
            var Q7;
            Q7=makeQuery(id+"F1.imprint","IMPRINT",FACE,{"disambiguationData":[TD([[makeQuery(id+"F1.imprint","IMPRINT",EDGE,{"derivedFrom":sQuery(id+"F1.wireOp",EDGE,"E62.0")}),-1.0]])]});
            var Q8;
            Q8=makeQuery(id+"F1.imprint","IMPRINT",FACE,{"disambiguationData":[TD([[makeQuery(id+"F1.imprint","IMPRINT",EDGE,{"derivedFrom":sQuery(id+"F1.wireOp",EDGE,"E17")}),1.0]])]});
            var Q9;
            Q9=makeQuery(id+"F1.imprint","IMPRINT",FACE,{"disambiguationData":[TD([[makeQuery(id+"F1.imprint","IMPRINT",EDGE,{"derivedFrom":sQuery(id+"F1.wireOp",EDGE,"E75")}),1.0]])]});
            extrude(context, id + "F4", {"entities" : qUnion([Q0, Q1, Q2, Q3, Q4, Q5, Q6, Q7, Q8, Q9]), "operationType" : NewBodyOperationType.REMOVE, "oppositeDirection" : true, "depth" : 2 * mm});
        }
        {
            var Q0;
            Q0=makeQuery(id+"F1.imprint","IMPRINT",FACE,{"disambiguationData":[TD([[makeQuery(id+"F1.imprint","IMPRINT",EDGE,{"derivedFrom":sQuery(id+"F1.wireOp",EDGE,"E108.0")}),-1.0]])]});
            extrude(context, id + "F5", {"entities" : qUnion([Q0]), "operationType" : NewBodyOperationType.REMOVE, "oppositeDirection" : true, "depth" : 2 * mm});
        }
        {
            var Q0;
            Q0=makeQuery(id+"F0.imprint","IMPRINT",FACE,{"disambiguationData":[TD([[makeQuery(id+"F0.imprint","IMPRINT",EDGE,{"derivedFrom":sQuery(id+"F0.wireOp",EDGE,"E1.0.2.0")}),1.0]])]});
            var Q1;
            Q1=makeQuery(id+"F0.imprint","IMPRINT",FACE,{"disambiguationData":[TD([[makeQuery(id+"F0.imprint","IMPRINT",EDGE,{"derivedFrom":sQuery(id+"F0.wireOp",EDGE,"E1.1.2.0")}),1.0]])]});
            var Q2;
            Q2=makeQuery(id+"F0.imprint","IMPRINT",FACE,{"disambiguationData":[TD([[makeQuery(id+"F0.imprint","IMPRINT",EDGE,{"derivedFrom":sQuery(id+"F0.wireOp",EDGE,"E1.2.2.0")}),1.0]])]});
            var Q3;
            Q3=makeQuery(id+"F0.imprint","IMPRINT",FACE,{"disambiguationData":[TD([[makeQuery(id+"F0.imprint","IMPRINT",EDGE,{"derivedFrom":sQuery(id+"F0.wireOp",EDGE,"E1.2.1.0")}),1.0]])]});
            var Q4;
            Q4=makeQuery(id+"F0.imprint","IMPRINT",FACE,{"disambiguationData":[TD([[makeQuery(id+"F0.imprint","IMPRINT",EDGE,{"derivedFrom":sQuery(id+"F0.wireOp",EDGE,"E1.1.1.0")}),1.0]])]});
            var Q5;
            Q5=makeQuery(id+"F0.imprint","IMPRINT",FACE,{"disambiguationData":[TD([[makeQuery(id+"F0.imprint","IMPRINT",EDGE,{"derivedFrom":sQuery(id+"F0.wireOp",EDGE,"E1.0.1.0")}),1.0]])]});
            var Q6;
            Q6=makeQuery(id+"F0.imprint","IMPRINT",FACE,{"disambiguationData":[TD([[makeQuery(id+"F0.imprint","IMPRINT",EDGE,{"derivedFrom":sQuery(id+"F0.wireOp",EDGE,"E0.rect.bottom")}),-1.0]])]});
            var Q7;
            Q7=makeQuery(id+"F0.imprint","IMPRINT",FACE,{"disambiguationData":[TD([[makeQuery(id+"F0.imprint","IMPRINT",EDGE,{"derivedFrom":sQuery(id+"F0.wireOp",EDGE,"E1.1.0.0")}),1.0]])]});
            var Q8;
            Q8=makeQuery(id+"F0.imprint","IMPRINT",FACE,{"disambiguationData":[TD([[makeQuery(id+"F0.imprint","IMPRINT",EDGE,{"derivedFrom":sQuery(id+"F0.wireOp",EDGE,"E1.2.0.0")}),1.0]])]});
            var Q9;
            Q9=makeQuery(id+"F0.imprint","IMPRINT",FACE,{"disambiguationData":[TD([[makeQuery(id+"F0.imprint","IMPRINT",EDGE,{"derivedFrom":sQuery(id+"F0.wireOp",EDGE,"E7.0.0.3")}),1.0]])]});
            var Q10;
            Q10=makeQuery(id+"F0.imprint","IMPRINT",FACE,{"disambiguationData":[TD([[makeQuery(id+"F0.imprint","IMPRINT",EDGE,{"derivedFrom":sQuery(id+"F0.wireOp",EDGE,"E7.0.1.3")}),1.0]])]});
            var Q11;
            Q11=makeQuery(id+"F0.imprint","IMPRINT",FACE,{"disambiguationData":[TD([[makeQuery(id+"F0.imprint","IMPRINT",EDGE,{"derivedFrom":sQuery(id+"F0.wireOp",EDGE,"E7.0.2.3")}),1.0]])]});
            extrude(context, id + "F6", {"entities" : qUnion([Q0, Q1, Q2, Q3, Q4, Q5, Q6, Q7, Q8, Q9, Q10, Q11]), "operationType" : NewBodyOperationType.ADD, "oppositeDirection" : true, "depth" : 9 * mm, "hasSecondDirection" : true, "secondDirectionOppositeDirection" : false, "secondDirectionDepth" : 1 * mm});
        }
        {
            var Q0;
            Q0=makeQuery(id+"F4.boolean.opBoolean","COPY",EDGE,{"derivedFrom":makeQuery(id+"F4.opExtrude","CAP_EDGE",EDGE,{"disambiguationData":[OSD([sQuery(id+"F1.wireOp",EDGE,"E16")])],"isStart":false})});
            var Q1;
            Q1=makeQuery(id+"F4.boolean.opBoolean","COPY",EDGE,{"derivedFrom":makeQuery(id+"F4.opExtrude","CAP_EDGE",EDGE,{"disambiguationData":[OSD([sQuery(id+"F1.wireOp",EDGE,"E17")])],"isStart":false})});
            var Q2;
            Q2=makeQuery(id+"F4.boolean.opBoolean","COPY",EDGE,{"derivedFrom":makeQuery(id+"F4.opExtrude","CAP_EDGE",EDGE,{"disambiguationData":[OSD([sQuery(id+"F1.wireOp",EDGE,"E18")])],"isStart":false})});
            var Q3;
            Q3=makeQuery(id+"F4.boolean.opBoolean","COPY",EDGE,{"derivedFrom":makeQuery(id+"F4.opExtrude","CAP_EDGE",EDGE,{"disambiguationData":[OSD([sQuery(id+"F1.wireOp",EDGE,"E14.filletArc")])],"isStart":false})});
            var Q4;
            Q4=makeQuery(id+"F4.boolean.opBoolean","COPY",EDGE,{"derivedFrom":makeQuery(id+"F4.opExtrude","CAP_EDGE",EDGE,{"disambiguationData":[OSD([sQuery(id+"F1.wireOp",EDGE,"E25.trimOffspring")])],"isStart":false})});
            var Q5;
            Q5=makeQuery(id+"F4.boolean.opBoolean","COPY",EDGE,{"derivedFrom":makeQuery(id+"F4.opExtrude","CAP_EDGE",EDGE,{"disambiguationData":[OSD([sQuery(id+"F1.wireOp",EDGE,"E62.4")])],"isStart":false})});
            var Q6;
            Q6=makeQuery(id+"F4.boolean.opBoolean","COPY",EDGE,{"derivedFrom":makeQuery(id+"F4.opExtrude","CAP_EDGE",EDGE,{"disambiguationData":[OSD([sQuery(id+"F1.wireOp",EDGE,"E56.3")])],"isStart":false})});
            var Q7;
            Q7=makeQuery(id+"F4.boolean.opBoolean","COPY",EDGE,{"derivedFrom":makeQuery(id+"F4.opExtrude","CAP_EDGE",EDGE,{"disambiguationData":[OSD([sQuery(id+"F1.wireOp",EDGE,"E44.2")])],"isStart":false})});
            var Q8;
            Q8=makeQuery(id+"F4.boolean.opBoolean","COPY",EDGE,{"derivedFrom":makeQuery(id+"F4.opExtrude","CAP_EDGE",EDGE,{"disambiguationData":[OSD([sQuery(id+"F1.wireOp",EDGE,"E49.4")])],"isStart":false})});
            var Q9;
            Q9=makeQuery(id+"F4.boolean.opBoolean","COPY",EDGE,{"derivedFrom":makeQuery(id+"F4.opExtrude","CAP_EDGE",EDGE,{"disambiguationData":[OSD([sQuery(id+"F1.wireOp",EDGE,"E10.0")])],"isStart":false})});
            var Q10;
            Q10=makeQuery(id+"F4.boolean.opBoolean","COPY",EDGE,{"derivedFrom":makeQuery(id+"F4.opExtrude","CAP_EDGE",EDGE,{"disambiguationData":[OSD([sQuery(id+"F1.wireOp",EDGE,"E77.trimOffspring")])],"isStart":false})});
            var Q11;
            Q11=makeQuery(id+"F3.boolean.opBoolean","COPY",EDGE,{"derivedFrom":makeQuery(id+"F3.opExtrude","CAP_EDGE",EDGE,{"disambiguationData":[OSD([sQuery(id+"F1.wireOp",EDGE,"E91")])],"isStart":false})});
            var Q12;
            Q12=makeQuery(id+"F3.boolean.opBoolean","COPY",EDGE,{"derivedFrom":makeQuery(id+"F3.opExtrude","CAP_EDGE",EDGE,{"disambiguationData":[OSD([sQuery(id+"F1.wireOp",EDGE,"E92")])],"isStart":false})});
            var Q13;
            Q13=makeQuery(id+"F3.boolean.opBoolean","COPY",EDGE,{"derivedFrom":makeQuery(id+"F3.opExtrude","CAP_EDGE",EDGE,{"disambiguationData":[OSD([sQuery(id+"F1.wireOp",EDGE,"E93")])],"isStart":false})});
            var Q14;
            Q14=makeQuery(id+"F3.boolean.opBoolean","COPY",EDGE,{"derivedFrom":makeQuery(id+"F3.opExtrude","CAP_EDGE",EDGE,{"disambiguationData":[OSD([sQuery(id+"F1.wireOp",EDGE,"E94")])],"isStart":false})});
            var Q15;
            Q15=makeQuery(id+"F3.boolean.opBoolean","COPY",EDGE,{"derivedFrom":makeQuery(id+"F3.opExtrude","CAP_EDGE",EDGE,{"disambiguationData":[OSD([sQuery(id+"F1.wireOp",EDGE,"E97")])],"isStart":false})});
            var Q16;
            Q16=makeQuery(id+"F3.boolean.opBoolean","COPY",EDGE,{"derivedFrom":makeQuery(id+"F3.opExtrude","CAP_EDGE",EDGE,{"disambiguationData":[OSD([sQuery(id+"F1.wireOp",EDGE,"E90")])],"isStart":false})});
            var Q17;
            Q17=makeQuery(id+"F3.boolean.opBoolean","COPY",EDGE,{"derivedFrom":makeQuery(id+"F3.opExtrude","CAP_EDGE",EDGE,{"disambiguationData":[OSD([sQuery(id+"F1.wireOp",EDGE,"E95")])],"isStart":false})});
            var Q18;
            Q18=makeQuery(id+"F3.boolean.opBoolean","COPY",EDGE,{"derivedFrom":makeQuery(id+"F3.opExtrude","CAP_EDGE",EDGE,{"disambiguationData":[OSD([sQuery(id+"F1.wireOp",EDGE,"E96")])],"isStart":false})});
            var Q19;
            Q19=makeQuery(id+"F3.boolean.opBoolean","COPY",EDGE,{"derivedFrom":makeQuery(id+"F3.opExtrude","CAP_EDGE",EDGE,{"disambiguationData":[OSD([sQuery(id+"F1.wireOp",EDGE,"E88")])],"isStart":false})});
            var Q20;
            Q20=makeQuery(id+"F5.boolean.opBoolean","COPY",EDGE,{"derivedFrom":makeQuery(id+"F5.opExtrude","CAP_EDGE",EDGE,{"disambiguationData":[OSD([sQuery(id+"F1.wireOp",EDGE,"E122.trimOffspring")])],"isStart":false})});
            var Q21;
            Q21=makeQuery(id+"F5.boolean.opBoolean","COPY",EDGE,{"derivedFrom":makeQuery(id+"F5.opExtrude","CAP_EDGE",EDGE,{"disambiguationData":[OSD([sQuery(id+"F1.wireOp",EDGE,"E112.MirrorC")])],"isStart":false})});
            var Q22;
            Q22=makeQuery(id+"F5.boolean.opBoolean","COPY",EDGE,{"derivedFrom":makeQuery(id+"F5.opExtrude","CAP_EDGE",EDGE,{"disambiguationData":[OSD([sQuery(id+"F1.wireOp",EDGE,"E116")])],"isStart":false})});
            var Q23;
            Q23=makeQuery(id+"F5.boolean.opBoolean","COPY",EDGE,{"derivedFrom":makeQuery(id+"F5.opExtrude","CAP_EDGE",EDGE,{"disambiguationData":[OSD([sQuery(id+"F1.wireOp",EDGE,"E111.MirrorC")])],"isStart":false})});
            var Q24;
            Q24=makeQuery(id+"F3.boolean.opBoolean","COPY",EDGE,{"derivedFrom":makeQuery(id+"F3.opExtrude","CAP_EDGE",EDGE,{"disambiguationData":[OSD([sQuery(id+"F1.wireOp",EDGE,"E87")])],"isStart":false})});
            var Q25;
            Q25=makeQuery(id+"F3.boolean.opBoolean","COPY",EDGE,{"derivedFrom":makeQuery(id+"F3.opExtrude","CAP_EDGE",EDGE,{"disambiguationData":[OSD([sQuery(id+"F1.wireOp",EDGE,"E89")])],"isStart":false})});
            var Q26;
            Q26=makeQuery(id+"F3.boolean.opBoolean","COPY",EDGE,{"derivedFrom":makeQuery(id+"F3.opExtrude","CAP_EDGE",EDGE,{"disambiguationData":[OSD([sQuery(id+"F1.wireOp",EDGE,"E86")])],"isStart":false})});
            fillet(context, id + "F7", {"entities" : qUnion([Q0, Q1, Q2, Q3, Q4, Q5, Q6, Q7, Q8, Q9, Q10, Q11, Q12, Q13, Q14, Q15, Q16, Q17, Q18, Q19, Q20, Q21, Q22, Q23, Q24, Q25, Q26]), "radius" : 0.5 * mm, "tangentPropagation" : true, "allowEdgeOverflow" : false});
        }
        {
            var Q0;
            Q0=makeQuery(id+"F7.opFillet","BLEND_EDGE",EDGE,{"blendedFrom":[makeQuery(id+"F3.boolean.opBoolean","COPY",EDGE,{"derivedFrom":makeQuery(id+"F3.opExtrude","CAP_EDGE",EDGE,{"disambiguationData":[OSD([sQuery(id+"F1.wireOp",EDGE,"E93")])],"isStart":false})}),makeQuery(id+"F3.boolean.opBoolean","COPY",EDGE,{"derivedFrom":makeQuery(id+"F3.opExtrude","CAP_EDGE",EDGE,{"disambiguationData":[OSD([sQuery(id+"F1.wireOp",EDGE,"E94")])],"isStart":false})})],"blendedInto":[]});
            var Q1;
            Q1=makeQuery(id+"F7.opFillet","BLEND_EDGE",EDGE,{"blendedFrom":[makeQuery(id+"F3.boolean.opBoolean","COPY",EDGE,{"derivedFrom":makeQuery(id+"F3.opExtrude","CAP_EDGE",EDGE,{"disambiguationData":[OSD([sQuery(id+"F1.wireOp",EDGE,"E96")])],"isStart":false})}),makeQuery(id+"F3.boolean.opBoolean","COPY",EDGE,{"derivedFrom":makeQuery(id+"F3.opExtrude","CAP_EDGE",EDGE,{"disambiguationData":[OSD([sQuery(id+"F1.wireOp",EDGE,"E97")])],"isStart":false})})],"blendedInto":[]});
            var Q2;
            Q2=makeQuery(id+"F7.opFillet","BLEND_EDGE",EDGE,{"blendedFrom":[makeQuery(id+"F3.boolean.opBoolean","COPY",EDGE,{"derivedFrom":makeQuery(id+"F3.opExtrude","CAP_EDGE",EDGE,{"disambiguationData":[OSD([sQuery(id+"F1.wireOp",EDGE,"E87")])],"isStart":false})}),makeQuery(id+"F3.boolean.opBoolean","COPY",EDGE,{"derivedFrom":makeQuery(id+"F3.opExtrude","CAP_EDGE",EDGE,{"disambiguationData":[OSD([sQuery(id+"F1.wireOp",EDGE,"E88")])],"isStart":false})})],"blendedInto":[]});
            var Q3;
            Q3=makeQuery(id+"F7.opFillet","BLEND_EDGE",EDGE,{"blendedFrom":[makeQuery(id+"F3.boolean.opBoolean","COPY",EDGE,{"derivedFrom":makeQuery(id+"F3.opExtrude","CAP_EDGE",EDGE,{"disambiguationData":[OSD([sQuery(id+"F1.wireOp",EDGE,"E90")])],"isStart":false})}),makeQuery(id+"F3.boolean.opBoolean","COPY",EDGE,{"derivedFrom":makeQuery(id+"F3.opExtrude","CAP_EDGE",EDGE,{"disambiguationData":[OSD([sQuery(id+"F1.wireOp",EDGE,"E91")])],"isStart":false})})],"blendedInto":[]});
            var Q4;
            Q4=makeQuery(id+"F7.opFillet","BLEND_EDGE",EDGE,{"blendedFrom":[makeQuery(id+"F5.boolean.opBoolean","COPY",EDGE,{"derivedFrom":makeQuery(id+"F5.opExtrude","CAP_EDGE",EDGE,{"disambiguationData":[OSD([sQuery(id+"F1.wireOp",EDGE,"E116")])],"isStart":false})}),makeQuery(id+"F5.boolean.opBoolean","COPY",EDGE,{"derivedFrom":makeQuery(id+"F5.opExtrude","CAP_EDGE",EDGE,{"disambiguationData":[OSD([sQuery(id+"F1.wireOp",EDGE,"E120.trimOffspring")])],"isStart":false})})],"blendedInto":[]});
            var Q5;
            Q5=makeQuery(id+"F7.opFillet","BLEND_EDGE",EDGE,{"blendedFrom":[makeQuery(id+"F5.boolean.opBoolean","COPY",EDGE,{"derivedFrom":makeQuery(id+"F5.opExtrude","CAP_EDGE",EDGE,{"disambiguationData":[OSD([sQuery(id+"F1.wireOp",EDGE,"E114")])],"isStart":false})}),makeQuery(id+"F5.boolean.opBoolean","COPY",EDGE,{"derivedFrom":makeQuery(id+"F5.opExtrude","CAP_EDGE",EDGE,{"disambiguationData":[OSD([sQuery(id+"F1.wireOp",EDGE,"E121.trimOffspring")])],"isStart":false})})],"blendedInto":[]});
            var Q6;
            Q6=makeQuery(id+"F7.opFillet","BLEND_EDGE",EDGE,{"blendedFrom":[makeQuery(id+"F5.boolean.opBoolean","COPY",EDGE,{"derivedFrom":makeQuery(id+"F5.opExtrude","CAP_EDGE",EDGE,{"disambiguationData":[OSD([sQuery(id+"F1.wireOp",EDGE,"E117")])],"isStart":false})}),makeQuery(id+"F5.boolean.opBoolean","COPY",EDGE,{"derivedFrom":makeQuery(id+"F5.opExtrude","CAP_EDGE",EDGE,{"disambiguationData":[OSD([sQuery(id+"F1.wireOp",EDGE,"E118.trimOffspring")])],"isStart":false})})],"blendedInto":[]});
            var Q7;
            Q7=makeQuery(id+"F7.opFillet","BLEND_EDGE",EDGE,{"blendedFrom":[makeQuery(id+"F5.boolean.opBoolean","COPY",EDGE,{"derivedFrom":makeQuery(id+"F5.opExtrude","CAP_EDGE",EDGE,{"disambiguationData":[OSD([sQuery(id+"F1.wireOp",EDGE,"E115")])],"isStart":false})}),makeQuery(id+"F5.boolean.opBoolean","COPY",EDGE,{"derivedFrom":makeQuery(id+"F5.opExtrude","CAP_EDGE",EDGE,{"disambiguationData":[OSD([sQuery(id+"F1.wireOp",EDGE,"E119.trimOffspring")])],"isStart":false})})],"blendedInto":[]});
            var Q8;
            Q8=makeQuery(id+"F3.boolean.opBoolean","COPY",EDGE,{"derivedFrom":makeQuery(id+"F3.opExtrude","SWEPT_EDGE",EDGE,{"disambiguationData":[OSD([sQuery(id+"F1.wireOp",EDGE,"E94"),sQuery(id+"F1.wireOp",EDGE,"E95")])]})});
            var Q9;
            Q9=makeQuery(id+"F3.boolean.opBoolean","COPY",EDGE,{"derivedFrom":makeQuery(id+"F3.opExtrude","SWEPT_EDGE",EDGE,{"disambiguationData":[OSD([sQuery(id+"F1.wireOp",EDGE,"E86"),sQuery(id+"F1.wireOp",EDGE,"E97")])]})});
            var Q10;
            Q10=makeQuery(id+"F3.boolean.opBoolean","COPY",EDGE,{"derivedFrom":makeQuery(id+"F3.opExtrude","SWEPT_EDGE",EDGE,{"disambiguationData":[OSD([sQuery(id+"F1.wireOp",EDGE,"E95"),sQuery(id+"F1.wireOp",EDGE,"E96")])]})});
            var Q11;
            Q11=makeQuery(id+"F3.boolean.opBoolean","COPY",EDGE,{"derivedFrom":makeQuery(id+"F3.opExtrude","SWEPT_EDGE",EDGE,{"disambiguationData":[OSD([sQuery(id+"F1.wireOp",EDGE,"E89"),sQuery(id+"F1.wireOp",EDGE,"E90")])]})});
            var Q12;
            Q12=makeQuery(id+"F3.boolean.opBoolean","COPY",EDGE,{"derivedFrom":makeQuery(id+"F3.opExtrude","SWEPT_EDGE",EDGE,{"disambiguationData":[OSD([sQuery(id+"F1.wireOp",EDGE,"E88"),sQuery(id+"F1.wireOp",EDGE,"E89")])]})});
            var Q13;
            Q13=makeQuery(id+"F3.boolean.opBoolean","COPY",EDGE,{"derivedFrom":makeQuery(id+"F3.opExtrude","SWEPT_EDGE",EDGE,{"disambiguationData":[OSD([sQuery(id+"F1.wireOp",EDGE,"E91"),sQuery(id+"F1.wireOp",EDGE,"E92")])]})});
            var Q14;
            Q14=makeQuery(id+"F3.boolean.opBoolean","COPY",EDGE,{"derivedFrom":makeQuery(id+"F3.opExtrude","SWEPT_EDGE",EDGE,{"disambiguationData":[OSD([sQuery(id+"F1.wireOp",EDGE,"E92"),sQuery(id+"F1.wireOp",EDGE,"E93")])]})});
            var Q15;
            Q15=makeQuery(id+"F3.boolean.opBoolean","COPY",EDGE,{"derivedFrom":makeQuery(id+"F3.opExtrude","SWEPT_EDGE",EDGE,{"disambiguationData":[OSD([sQuery(id+"F1.wireOp",EDGE,"E86"),sQuery(id+"F1.wireOp",EDGE,"E87")])]})});
            fillet(context, id + "F8", {"entities" : qUnion([Q0, Q1, Q2, Q3, Q4, Q5, Q6, Q7, Q8, Q9, Q10, Q11, Q12, Q13, Q14, Q15]), "radius" : 0.5 * mm, "tangentPropagation" : true, "allowEdgeOverflow" : false});
        }
        {
            var Q0;
            Q0=makeQuery(id+"F6.opExtrude","SWEPT_EDGE",EDGE,{"disambiguationData":[OSD([sQuery(id+"F0.wireOp",EDGE,"E5.0"),sQuery(id+"F0.wireOp",EDGE,"E5.3")])]});
            var Q1;
            Q1=makeQuery(id+"F6.opExtrude","SWEPT_EDGE",EDGE,{"disambiguationData":[OSD([sQuery(id+"F0.wireOp",EDGE,"E5.2"),sQuery(id+"F0.wireOp",EDGE,"E5.3")])]});
            var Q2;
            Q2=makeQuery(id+"F6.opExtrude","SWEPT_EDGE",EDGE,{"disambiguationData":[OSD([sQuery(id+"F0.wireOp",EDGE,"E6.1.0.0"),sQuery(id+"F0.wireOp",EDGE,"E6.1.0.1")])]});
            var Q3;
            Q3=makeQuery(id+"F6.opExtrude","SWEPT_EDGE",EDGE,{"disambiguationData":[OSD([sQuery(id+"F0.wireOp",EDGE,"E6.1.0.1"),sQuery(id+"F0.wireOp",EDGE,"E6.1.0.2")])]});
            var Q4;
            Q4=makeQuery(id+"F6.opExtrude","SWEPT_EDGE",EDGE,{"disambiguationData":[OSD([sQuery(id+"F0.wireOp",EDGE,"E6.2.0.0"),sQuery(id+"F0.wireOp",EDGE,"E6.2.0.1")])]});
            var Q5;
            Q5=makeQuery(id+"F6.opExtrude","SWEPT_EDGE",EDGE,{"disambiguationData":[OSD([sQuery(id+"F0.wireOp",EDGE,"E6.2.0.1"),sQuery(id+"F0.wireOp",EDGE,"E6.2.0.2")])]});
            var Q6;
            Q6=makeQuery(id+"F6.opExtrude","SWEPT_EDGE",EDGE,{"disambiguationData":[OSD([sQuery(id+"F0.wireOp",EDGE,"E6.2.0.2"),sQuery(id+"F0.wireOp",EDGE,"E6.2.0.3")])]});
            var Q7;
            Q7=makeQuery(id+"F6.opExtrude","SWEPT_EDGE",EDGE,{"disambiguationData":[OSD([sQuery(id+"F0.wireOp",EDGE,"E6.2.1.1"),sQuery(id+"F0.wireOp",EDGE,"E6.2.1.2")])]});
            var Q8;
            Q8=makeQuery(id+"F6.opExtrude","SWEPT_EDGE",EDGE,{"disambiguationData":[OSD([sQuery(id+"F0.wireOp",EDGE,"E6.2.1.2"),sQuery(id+"F0.wireOp",EDGE,"E6.2.1.3")])]});
            var Q9;
            Q9=makeQuery(id+"F6.opExtrude","SWEPT_EDGE",EDGE,{"disambiguationData":[OSD([sQuery(id+"F0.wireOp",EDGE,"E6.2.2.1"),sQuery(id+"F0.wireOp",EDGE,"E6.2.2.2")])]});
            var Q10;
            Q10=makeQuery(id+"F6.opExtrude","SWEPT_EDGE",EDGE,{"disambiguationData":[OSD([sQuery(id+"F0.wireOp",EDGE,"E6.2.2.2"),sQuery(id+"F0.wireOp",EDGE,"E6.2.2.3")])]});
            var Q11;
            Q11=makeQuery(id+"F6.opExtrude","SWEPT_EDGE",EDGE,{"disambiguationData":[OSD([sQuery(id+"F0.wireOp",EDGE,"E8.3.2.3"),sQuery(id+"F0.wireOp",EDGE,"E8.6.2.3")])]});
            var Q12;
            Q12=makeQuery(id+"F6.opExtrude","SWEPT_EDGE",EDGE,{"disambiguationData":[OSD([sQuery(id+"F0.wireOp",EDGE,"E8.6.2.3"),sQuery(id+"F0.wireOp",EDGE,"E8.9.2.3")])]});
            var Q13;
            Q13=makeQuery(id+"F6.opExtrude","SWEPT_EDGE",EDGE,{"disambiguationData":[OSD([sQuery(id+"F0.wireOp",EDGE,"E6.1.1.1"),sQuery(id+"F0.wireOp",EDGE,"E6.1.1.2")])]});
            var Q14;
            Q14=makeQuery(id+"F6.opExtrude","SWEPT_EDGE",EDGE,{"disambiguationData":[OSD([sQuery(id+"F0.wireOp",EDGE,"E6.1.0.2"),sQuery(id+"F0.wireOp",EDGE,"E6.1.0.3")])]});
            var Q15;
            Q15=makeQuery(id+"F6.opExtrude","SWEPT_EDGE",EDGE,{"disambiguationData":[OSD([sQuery(id+"F0.wireOp",EDGE,"E6.2.1.0"),sQuery(id+"F0.wireOp",EDGE,"E6.2.1.1")])]});
            var Q16;
            Q16=makeQuery(id+"F6.opExtrude","SWEPT_EDGE",EDGE,{"disambiguationData":[OSD([sQuery(id+"F0.wireOp",EDGE,"E6.2.2.0"),sQuery(id+"F0.wireOp",EDGE,"E6.2.2.1")])]});
            var Q17;
            Q17=makeQuery(id+"F6.opExtrude","SWEPT_EDGE",EDGE,{"disambiguationData":[OSD([sQuery(id+"F0.wireOp",EDGE,"E6.1.2.1"),sQuery(id+"F0.wireOp",EDGE,"E6.1.2.2")])]});
            var Q18;
            Q18=makeQuery(id+"F6.opExtrude","SWEPT_EDGE",EDGE,{"disambiguationData":[OSD([sQuery(id+"F0.wireOp",EDGE,"E6.1.1.2"),sQuery(id+"F0.wireOp",EDGE,"E6.1.1.3")])]});
            var Q19;
            Q19=makeQuery(id+"F6.opExtrude","SWEPT_EDGE",EDGE,{"disambiguationData":[OSD([sQuery(id+"F0.wireOp",EDGE,"E6.1.2.2"),sQuery(id+"F0.wireOp",EDGE,"E6.1.2.3")])]});
            var Q20;
            Q20=makeQuery(id+"F6.opExtrude","SWEPT_EDGE",EDGE,{"disambiguationData":[OSD([sQuery(id+"F0.wireOp",EDGE,"E8.3.1.3"),sQuery(id+"F0.wireOp",EDGE,"E8.6.1.3")])]});
            var Q21;
            Q21=makeQuery(id+"F6.opExtrude","SWEPT_EDGE",EDGE,{"disambiguationData":[OSD([sQuery(id+"F0.wireOp",EDGE,"E8.0.2.3"),sQuery(id+"F0.wireOp",EDGE,"E8.3.2.3")])]});
            var Q22;
            Q22=makeQuery(id+"F6.opExtrude","SWEPT_EDGE",EDGE,{"disambiguationData":[OSD([sQuery(id+"F0.wireOp",EDGE,"E8.6.1.3"),sQuery(id+"F0.wireOp",EDGE,"E8.9.1.3")])]});
            var Q23;
            Q23=makeQuery(id+"F6.opExtrude","SWEPT_EDGE",EDGE,{"disambiguationData":[OSD([sQuery(id+"F0.wireOp",EDGE,"E8.6.0.3"),sQuery(id+"F0.wireOp",EDGE,"E8.9.0.3")])]});
            var Q24;
            Q24=makeQuery(id+"F6.opExtrude","SWEPT_EDGE",EDGE,{"disambiguationData":[OSD([sQuery(id+"F0.wireOp",EDGE,"E8.0.1.3"),sQuery(id+"F0.wireOp",EDGE,"E8.3.1.3")])]});
            var Q25;
            Q25=makeQuery(id+"F6.opExtrude","SWEPT_EDGE",EDGE,{"disambiguationData":[OSD([sQuery(id+"F0.wireOp",EDGE,"E8.3.0.3"),sQuery(id+"F0.wireOp",EDGE,"E8.6.0.3")])]});
            var Q26;
            Q26=makeQuery(id+"F6.opExtrude","SWEPT_EDGE",EDGE,{"disambiguationData":[OSD([sQuery(id+"F0.wireOp",EDGE,"E6.1.2.0"),sQuery(id+"F0.wireOp",EDGE,"E6.1.2.1")])]});
            var Q27;
            Q27=makeQuery(id+"F6.opExtrude","SWEPT_EDGE",EDGE,{"disambiguationData":[OSD([sQuery(id+"F0.wireOp",EDGE,"E6.0.2.1"),sQuery(id+"F0.wireOp",EDGE,"E6.0.2.2")])]});
            var Q28;
            Q28=makeQuery(id+"F6.opExtrude","SWEPT_EDGE",EDGE,{"disambiguationData":[OSD([sQuery(id+"F0.wireOp",EDGE,"E6.0.1.2"),sQuery(id+"F0.wireOp",EDGE,"E6.0.1.3")])]});
            var Q29;
            Q29=makeQuery(id+"F6.opExtrude","SWEPT_EDGE",EDGE,{"disambiguationData":[OSD([sQuery(id+"F0.wireOp",EDGE,"E6.1.1.0"),sQuery(id+"F0.wireOp",EDGE,"E6.1.1.1")])]});
            var Q30;
            Q30=makeQuery(id+"F6.opExtrude","SWEPT_EDGE",EDGE,{"disambiguationData":[OSD([sQuery(id+"F0.wireOp",EDGE,"E6.0.1.1"),sQuery(id+"F0.wireOp",EDGE,"E6.0.1.2")])]});
            var Q31;
            Q31=makeQuery(id+"F6.opExtrude","SWEPT_EDGE",EDGE,{"disambiguationData":[OSD([sQuery(id+"F0.wireOp",EDGE,"E5.1"),sQuery(id+"F0.wireOp",EDGE,"E5.2")])]});
            var Q32;
            Q32=makeQuery(id+"F6.opExtrude","SWEPT_EDGE",EDGE,{"disambiguationData":[OSD([sQuery(id+"F0.wireOp",EDGE,"E6.0.1.0"),sQuery(id+"F0.wireOp",EDGE,"E6.0.1.1")])]});
            var Q33;
            Q33=makeQuery(id+"F6.opExtrude","SWEPT_EDGE",EDGE,{"disambiguationData":[OSD([sQuery(id+"F0.wireOp",EDGE,"E6.0.2.0"),sQuery(id+"F0.wireOp",EDGE,"E6.0.2.1")])]});
            var Q34;
            Q34=makeQuery(id+"F6.opExtrude","SWEPT_EDGE",EDGE,{"disambiguationData":[OSD([sQuery(id+"F0.wireOp",EDGE,"E8.0.0.3"),sQuery(id+"F0.wireOp",EDGE,"E8.3.0.3")])]});
            var Q35;
            Q35=makeQuery(id+"F6.opExtrude","SWEPT_EDGE",EDGE,{"disambiguationData":[OSD([sQuery(id+"F0.wireOp",EDGE,"E8.0.0.3"),sQuery(id+"F0.wireOp",EDGE,"E8.9.0.3")])]});
            var Q36;
            Q36=makeQuery(id+"F6.opExtrude","SWEPT_EDGE",EDGE,{"disambiguationData":[OSD([sQuery(id+"F0.wireOp",EDGE,"E8.0.1.3"),sQuery(id+"F0.wireOp",EDGE,"E8.9.1.3")])]});
            var Q37;
            Q37=makeQuery(id+"F6.opExtrude","SWEPT_EDGE",EDGE,{"disambiguationData":[OSD([sQuery(id+"F0.wireOp",EDGE,"E6.1.2.0"),sQuery(id+"F0.wireOp",EDGE,"E6.1.2.3")])]});
            var Q38;
            Q38=makeQuery(id+"F6.opExtrude","SWEPT_EDGE",EDGE,{"disambiguationData":[OSD([sQuery(id+"F0.wireOp",EDGE,"E6.1.1.0"),sQuery(id+"F0.wireOp",EDGE,"E6.1.1.3")])]});
            var Q39;
            Q39=makeQuery(id+"F6.opExtrude","SWEPT_EDGE",EDGE,{"disambiguationData":[OSD([sQuery(id+"F0.wireOp",EDGE,"E6.1.0.0"),sQuery(id+"F0.wireOp",EDGE,"E6.1.0.3")])]});
            var Q40;
            Q40=makeQuery(id+"F6.opExtrude","SWEPT_EDGE",EDGE,{"disambiguationData":[OSD([sQuery(id+"F0.wireOp",EDGE,"E6.2.0.0"),sQuery(id+"F0.wireOp",EDGE,"E6.2.0.3")])]});
            var Q41;
            Q41=makeQuery(id+"F6.opExtrude","SWEPT_EDGE",EDGE,{"disambiguationData":[OSD([sQuery(id+"F0.wireOp",EDGE,"E6.2.1.0"),sQuery(id+"F0.wireOp",EDGE,"E6.2.1.3")])]});
            var Q42;
            Q42=makeQuery(id+"F6.opExtrude","SWEPT_EDGE",EDGE,{"disambiguationData":[OSD([sQuery(id+"F0.wireOp",EDGE,"E6.2.2.0"),sQuery(id+"F0.wireOp",EDGE,"E6.2.2.3")])]});
            var Q43;
            Q43=makeQuery(id+"F6.opExtrude","SWEPT_EDGE",EDGE,{"disambiguationData":[OSD([sQuery(id+"F0.wireOp",EDGE,"E6.0.2.2"),sQuery(id+"F0.wireOp",EDGE,"E6.0.2.3")])]});
            var Q44;
            Q44=makeQuery(id+"F6.opExtrude","SWEPT_EDGE",EDGE,{"disambiguationData":[OSD([sQuery(id+"F0.wireOp",EDGE,"E8.0.2.3"),sQuery(id+"F0.wireOp",EDGE,"E8.9.2.3")])]});
            var Q45;
            Q45=makeQuery(id+"F6.opExtrude","SWEPT_EDGE",EDGE,{"disambiguationData":[OSD([sQuery(id+"F0.wireOp",EDGE,"E6.0.1.0"),sQuery(id+"F0.wireOp",EDGE,"E6.0.1.3")])]});
            var Q46;
            Q46=makeQuery(id+"F6.opExtrude","SWEPT_EDGE",EDGE,{"disambiguationData":[OSD([sQuery(id+"F0.wireOp",EDGE,"E5.0"),sQuery(id+"F0.wireOp",EDGE,"E5.1")])]});
            var Q47;
            Q47=makeQuery(id+"F6.opExtrude","SWEPT_EDGE",EDGE,{"disambiguationData":[OSD([sQuery(id+"F0.wireOp",EDGE,"E6.0.2.0"),sQuery(id+"F0.wireOp",EDGE,"E6.0.2.3")])]});
            fillet(context, id + "F9", {"entities" : qUnion([Q0, Q1, Q2, Q3, Q4, Q5, Q6, Q7, Q8, Q9, Q10, Q11, Q12, Q13, Q14, Q15, Q16, Q17, Q18, Q19, Q20, Q21, Q22, Q23, Q24, Q25, Q26, Q27, Q28, Q29, Q30, Q31, Q32, Q33, Q34, Q35, Q36, Q37, Q38, Q39, Q40, Q41, Q42, Q43, Q44, Q45, Q46, Q47]), "radius" : 1 * mm, "tangentPropagation" : true, "allowEdgeOverflow" : false});
        }
    });
